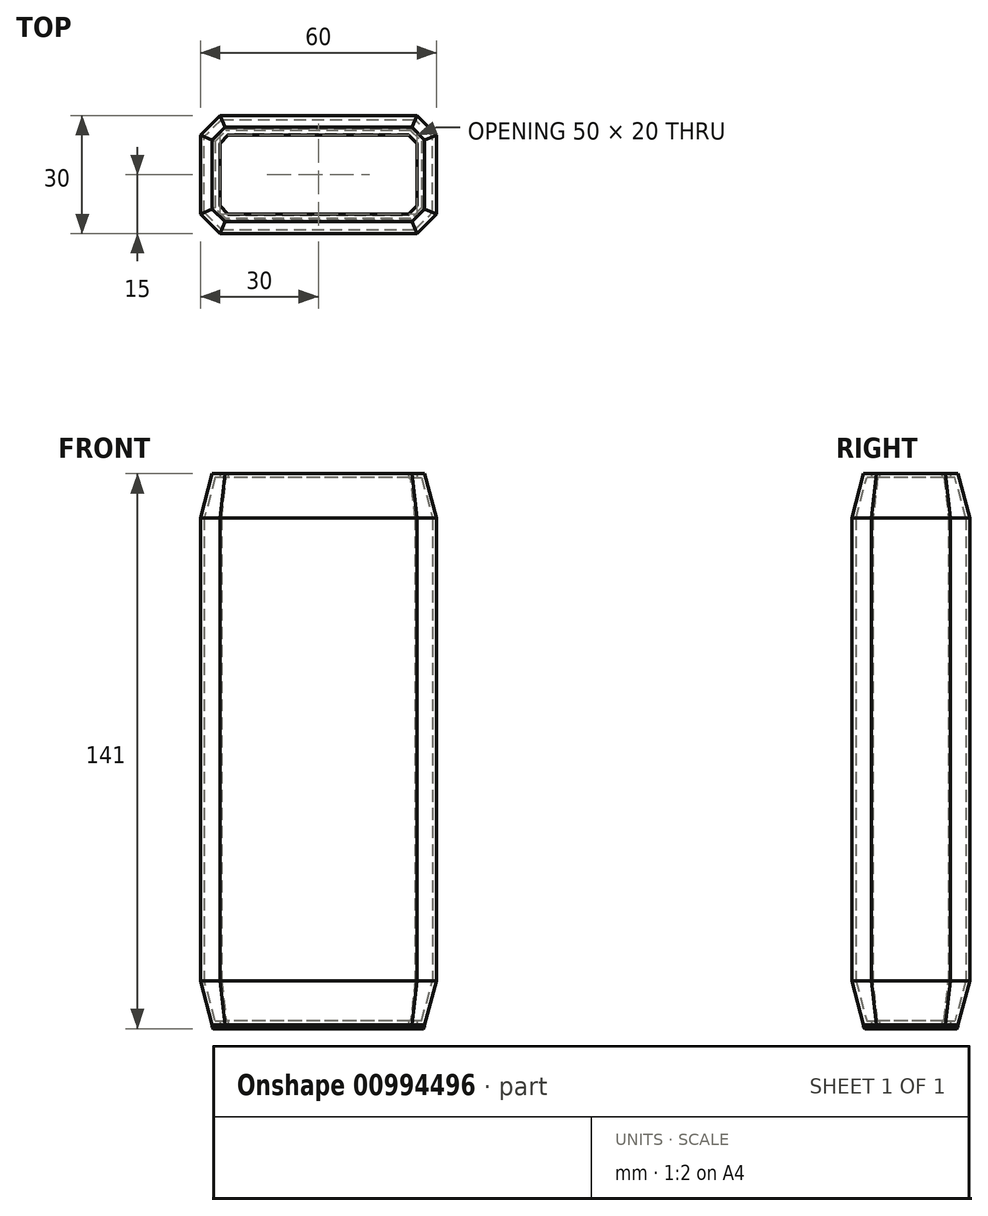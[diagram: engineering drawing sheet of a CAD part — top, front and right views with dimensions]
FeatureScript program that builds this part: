
annotation { "Feature Type Name" : "Feature", "Feature Type Description" : "" }
export const myFeature = defineFeature(function(context is Context, id is Id, definition is map)
    precondition{}
    {
        {
            var Q0;
            Q0=qCreatedBy(makeId("Top.planeOp"),FACE);
            var sketch = newSketch(context, id + "F0", { "sketchPlane" : qUnion([Q0])});
            skLineSegment(sketch, "E0.bottom", {"start": v(30, 15) * mm, "end": v(25, 15) * mm});
            skLineSegment(sketch, "E0.top", {"start": v(30, -15) * mm, "end": v(25, -15) * mm});
            skLineSegment(sketch, "E0.left", {"start": v(30, 15) * mm, "end": v(30, 10) * mm});
            skLineSegment(sketch, "E0.right", {"start": v(-30, 15) * mm, "end": v(-30, 10) * mm});
            skPoint(sketch, "E0.middle", {"position": v(0, 0) * mm});
            skPoint(sketch, "E1", {"position": v(-30, 0) * mm});
            skPoint(sketch, "E2", {"position": v(0, 15) * mm});
            skLineSegment(sketch, "E3", {"start": v(-30, 10) * mm, "end": v(-30, -10) * mm});
            skLineSegment(sketch, "E4", {"start": v(-25, 15) * mm, "end": v(-30, 15) * mm});
            skLineSegment(sketch, "E5", {"start": v(25, 15) * mm, "end": v(-25, 15) * mm});
            skLineSegment(sketch, "E6", {"start": v(30, 10) * mm, "end": v(30, -10) * mm});
            skLineSegment(sketch, "E7", {"start": v(30, -10) * mm, "end": v(30, -15) * mm});
            skLineSegment(sketch, "E8", {"start": v(25, -15) * mm, "end": v(-25, -15) * mm});
            skLineSegment(sketch, "E9", {"start": v(-25, -15) * mm, "end": v(-30, -15) * mm});
            skLineSegment(sketch, "E10", {"start": v(-30, -10) * mm, "end": v(-30, -15) * mm});
            skLineSegment(sketch, "E11", {"start": v(-30, 10) * mm, "end": v(-25, 15) * mm});
            skLineSegment(sketch, "E12", {"start": v(25, 15) * mm, "end": v(30, 10) * mm});
            skLineSegment(sketch, "E13", {"start": v(30, -10) * mm, "end": v(25, -15) * mm});
            skLineSegment(sketch, "E14", {"start": v(-25, -15) * mm, "end": v(-30, -10) * mm});
            skLineSegment(sketch, "E15.0", {"start": v(22.93, 10) * mm, "end": v(-22.93, 10) * mm});
            skLineSegment(sketch, "E15.1", {"start": v(-25, 7.93) * mm, "end": v(-22.93, 10) * mm});
            skLineSegment(sketch, "E15.2", {"start": v(22.93, 10) * mm, "end": v(25, 7.93) * mm});
            skLineSegment(sketch, "E15.3", {"start": v(-25, 7.93) * mm, "end": v(-25, -7.93) * mm});
            skLineSegment(sketch, "E15.4", {"start": v(25, 7.93) * mm, "end": v(25, -7.93) * mm});
            skLineSegment(sketch, "E15.5", {"start": v(25, -7.93) * mm, "end": v(22.93, -10) * mm});
            skLineSegment(sketch, "E15.6", {"start": v(22.93, -10) * mm, "end": v(-22.93, -10) * mm});
            skLineSegment(sketch, "E15.7", {"start": v(-22.93, -10) * mm, "end": v(-25, -7.93) * mm});
            skSolve(sketch);
        }
        {
            var Q0;
            Q0=makeQuery(id+"F0.imprint","IMPRINT",FACE,{"disambiguationData":[TD([[makeQuery(id+"F0.imprint","IMPRINT",EDGE,{"derivedFrom":sQuery(id+"F0.wireOp",EDGE,"E3")}),1.0]])]});
            extrude(context, id + "F1", {"entities" : qUnion([Q0]), "depth" : 70 * mm, "offsetDistance" : 25 * mm});
        }
        {
            var Q0;
            Q0=makeQuery(id+"F1.opExtrude","CAP_EDGE",EDGE,{"disambiguationData":[OSD([sQuery(id+"F0.wireOp",EDGE,"E3")])],"isStart":false});
            var Q1;
            Q1=makeQuery(id+"F1.opExtrude","CAP_EDGE",EDGE,{"disambiguationData":[OSD([sQuery(id+"F0.wireOp",EDGE,"E14")])],"isStart":false});
            var Q2;
            Q2=makeQuery(id+"F1.opExtrude","CAP_EDGE",EDGE,{"disambiguationData":[OSD([sQuery(id+"F0.wireOp",EDGE,"E8")])],"isStart":false});
            var Q3;
            Q3=makeQuery(id+"F1.opExtrude","CAP_EDGE",EDGE,{"disambiguationData":[OSD([sQuery(id+"F0.wireOp",EDGE,"E13")])],"isStart":false});
            var Q4;
            Q4=makeQuery(id+"F1.opExtrude","CAP_EDGE",EDGE,{"disambiguationData":[OSD([sQuery(id+"F0.wireOp",EDGE,"E6")])],"isStart":false});
            var Q5;
            Q5=makeQuery(id+"F1.opExtrude","CAP_EDGE",EDGE,{"disambiguationData":[OSD([sQuery(id+"F0.wireOp",EDGE,"E12")])],"isStart":false});
            var Q6;
            Q6=makeQuery(id+"F1.opExtrude","CAP_EDGE",EDGE,{"disambiguationData":[OSD([sQuery(id+"F0.wireOp",EDGE,"E5")])],"isStart":false});
            var Q7;
            Q7=makeQuery(id+"F1.opExtrude","CAP_EDGE",EDGE,{"disambiguationData":[OSD([sQuery(id+"F0.wireOp",EDGE,"E11")])],"isStart":false});
            chamfer(context, id + "F2", {"entities" : qUnion([Q0, Q1, Q2, Q3, Q4, Q5, Q6, Q7]), "chamferType" : ChamferType.OFFSET_ANGLE, "width" : 3 * mm, "oppositeDirection" : false, "angle" : 75 * degree, "tangentPropagation" : true});
        }
        {
            var Q0;
            Q0=makeQuery(id+"F1.opExtrude","SWEPT_BODY",BODY,{"disambiguationData":[OSD([sQuery(id+"F0.wireOp",EDGE,"E3"),sQuery(id+"F0.wireOp",EDGE,"E5"),sQuery(id+"F0.wireOp",EDGE,"E6"),sQuery(id+"F0.wireOp",EDGE,"E8"),sQuery(id+"F0.wireOp",EDGE,"E11"),sQuery(id+"F0.wireOp",EDGE,"E12"),sQuery(id+"F0.wireOp",EDGE,"E13"),sQuery(id+"F0.wireOp",EDGE,"E14"),sQuery(id+"F0.wireOp",EDGE,"E15.0"),sQuery(id+"F0.wireOp",EDGE,"E15.1"),sQuery(id+"F0.wireOp",EDGE,"E15.2"),sQuery(id+"F0.wireOp",EDGE,"E15.3"),sQuery(id+"F0.wireOp",EDGE,"E15.4"),sQuery(id+"F0.wireOp",EDGE,"E15.5"),sQuery(id+"F0.wireOp",EDGE,"E15.6"),sQuery(id+"F0.wireOp",EDGE,"E15.7")])]});
            var Q1;
            Q1=makeQuery(id+"F1.opExtrude","CAP_FACE",FACE,{"disambiguationData":[OSD([sQuery(id+"F0.wireOp",EDGE,"E3"),sQuery(id+"F0.wireOp",EDGE,"E5"),sQuery(id+"F0.wireOp",EDGE,"E6"),sQuery(id+"F0.wireOp",EDGE,"E8"),sQuery(id+"F0.wireOp",EDGE,"E11"),sQuery(id+"F0.wireOp",EDGE,"E12"),sQuery(id+"F0.wireOp",EDGE,"E13"),sQuery(id+"F0.wireOp",EDGE,"E14"),sQuery(id+"F0.wireOp",EDGE,"E15.0"),sQuery(id+"F0.wireOp",EDGE,"E15.1"),sQuery(id+"F0.wireOp",EDGE,"E15.2"),sQuery(id+"F0.wireOp",EDGE,"E15.3"),sQuery(id+"F0.wireOp",EDGE,"E15.4"),sQuery(id+"F0.wireOp",EDGE,"E15.5"),sQuery(id+"F0.wireOp",EDGE,"E15.6"),sQuery(id+"F0.wireOp",EDGE,"E15.7")])],"isStart":true});
            mirror(context, id + "F3", {"operationType" : NewBodyOperationType.ADD, "entities" : qUnion([Q0]), "mirrorPlane" : qUnion([Q1])});
        }
        {
            var Q0;
            {var subQ0=makeQuery(id+"F1.opExtrude","SWEPT_FACE",FACE,{"disambiguationData":[OSD([sQuery(id+"F0.wireOp",EDGE,"E15.3")])]});Q0=makeQuery(id+"F3.boolean.opBoolean","MERGE",FACE,{"derivedFrom":[subQ0,makeQuery(id+"F3.opPattern","COPY",FACE,{"derivedFrom":subQ0,"instanceName":"1"})]});}
            var Q1;
            {var subQ0=makeQuery(id+"F1.opExtrude","SWEPT_FACE",FACE,{"disambiguationData":[OSD([sQuery(id+"F0.wireOp",EDGE,"E15.1")])]});Q1=makeQuery(id+"F3.boolean.opBoolean","MERGE",FACE,{"derivedFrom":[subQ0,makeQuery(id+"F3.opPattern","COPY",FACE,{"derivedFrom":subQ0,"instanceName":"1"})]});}
            var Q2;
            {var subQ0=makeQuery(id+"F1.opExtrude","SWEPT_FACE",FACE,{"disambiguationData":[OSD([sQuery(id+"F0.wireOp",EDGE,"E15.0")])]});Q2=makeQuery(id+"F3.boolean.opBoolean","MERGE",FACE,{"derivedFrom":[subQ0,makeQuery(id+"F3.opPattern","COPY",FACE,{"derivedFrom":subQ0,"instanceName":"1"})]});}
            var Q3;
            {var subQ0=makeQuery(id+"F1.opExtrude","SWEPT_FACE",FACE,{"disambiguationData":[OSD([sQuery(id+"F0.wireOp",EDGE,"E15.2")])]});Q3=makeQuery(id+"F3.boolean.opBoolean","MERGE",FACE,{"derivedFrom":[subQ0,makeQuery(id+"F3.opPattern","COPY",FACE,{"derivedFrom":subQ0,"instanceName":"1"})]});}
            var Q4;
            {var subQ0=makeQuery(id+"F1.opExtrude","SWEPT_FACE",FACE,{"disambiguationData":[OSD([sQuery(id+"F0.wireOp",EDGE,"E15.4")])]});Q4=makeQuery(id+"F3.boolean.opBoolean","MERGE",FACE,{"derivedFrom":[subQ0,makeQuery(id+"F3.opPattern","COPY",FACE,{"derivedFrom":subQ0,"instanceName":"1"})]});}
            var Q5;
            {var subQ0=makeQuery(id+"F1.opExtrude","SWEPT_FACE",FACE,{"disambiguationData":[OSD([sQuery(id+"F0.wireOp",EDGE,"E15.6")])]});Q5=makeQuery(id+"F3.boolean.opBoolean","MERGE",FACE,{"derivedFrom":[subQ0,makeQuery(id+"F3.opPattern","COPY",FACE,{"derivedFrom":subQ0,"instanceName":"1"})]});}
            var Q6;
            {var subQ0=makeQuery(id+"F1.opExtrude","SWEPT_FACE",FACE,{"disambiguationData":[OSD([sQuery(id+"F0.wireOp",EDGE,"E15.7")])]});Q6=makeQuery(id+"F3.boolean.opBoolean","MERGE",FACE,{"derivedFrom":[subQ0,makeQuery(id+"F3.opPattern","COPY",FACE,{"derivedFrom":subQ0,"instanceName":"1"})]});}
            var Q7;
            {var subQ0=makeQuery(id+"F1.opExtrude","SWEPT_FACE",FACE,{"disambiguationData":[OSD([sQuery(id+"F0.wireOp",EDGE,"E15.5")])]});Q7=makeQuery(id+"F3.boolean.opBoolean","MERGE",FACE,{"derivedFrom":[subQ0,makeQuery(id+"F3.opPattern","COPY",FACE,{"derivedFrom":subQ0,"instanceName":"1"})]});}
            shell(context, id + "F4", {"entities" : qUnion([Q0, Q1, Q2, Q3, Q4, Q5, Q6, Q7]), "thickness" : 1 * mm});
        }
        {
            var Q0;
            Q0=makeQuery(id+"F3.opPattern","COPY",FACE,{"derivedFrom":makeQuery(id+"F1.opExtrude","CAP_FACE",FACE,{"disambiguationData":[OSD([sQuery(id+"F0.wireOp",EDGE,"E3"),sQuery(id+"F0.wireOp",EDGE,"E5"),sQuery(id+"F0.wireOp",EDGE,"E6"),sQuery(id+"F0.wireOp",EDGE,"E8"),sQuery(id+"F0.wireOp",EDGE,"E11"),sQuery(id+"F0.wireOp",EDGE,"E12"),sQuery(id+"F0.wireOp",EDGE,"E13"),sQuery(id+"F0.wireOp",EDGE,"E14"),sQuery(id+"F0.wireOp",EDGE,"E15.0"),sQuery(id+"F0.wireOp",EDGE,"E15.1"),sQuery(id+"F0.wireOp",EDGE,"E15.2"),sQuery(id+"F0.wireOp",EDGE,"E15.3"),sQuery(id+"F0.wireOp",EDGE,"E15.4"),sQuery(id+"F0.wireOp",EDGE,"E15.5"),sQuery(id+"F0.wireOp",EDGE,"E15.6"),sQuery(id+"F0.wireOp",EDGE,"E15.7")])],"isStart":false}),"instanceName":"1"});
            extrude(context, id + "F5", {"entities" : qUnion([Q0]), "operationType" : NewBodyOperationType.ADD, "depth" : 1 * mm, "offsetDistance" : 25 * mm});
        }
        {
            var Q0;
            Q0=makeQuery(id+"F5.opExtrude","CAP_FACE",FACE,{"disambiguationData":[OSD([sQuery(id+"F0.wireOp",EDGE,"E3"),sQuery(id+"F0.wireOp",EDGE,"E5"),sQuery(id+"F0.wireOp",EDGE,"E6"),sQuery(id+"F0.wireOp",EDGE,"E8"),sQuery(id+"F0.wireOp",EDGE,"E11"),sQuery(id+"F0.wireOp",EDGE,"E12"),sQuery(id+"F0.wireOp",EDGE,"E13"),sQuery(id+"F0.wireOp",EDGE,"E14"),sQuery(id+"F0.wireOp",EDGE,"E15.0"),sQuery(id+"F0.wireOp",EDGE,"E15.1"),sQuery(id+"F0.wireOp",EDGE,"E15.2"),sQuery(id+"F0.wireOp",EDGE,"E15.3"),sQuery(id+"F0.wireOp",EDGE,"E15.4"),sQuery(id+"F0.wireOp",EDGE,"E15.5"),sQuery(id+"F0.wireOp",EDGE,"E15.6"),sQuery(id+"F0.wireOp",EDGE,"E15.7")])],"isStart":false});
            chamfer(context, id + "F6", {"entities" : qUnion([Q0]), "width" : .3 * mm, "tangentPropagation" : true});
        }
    });
